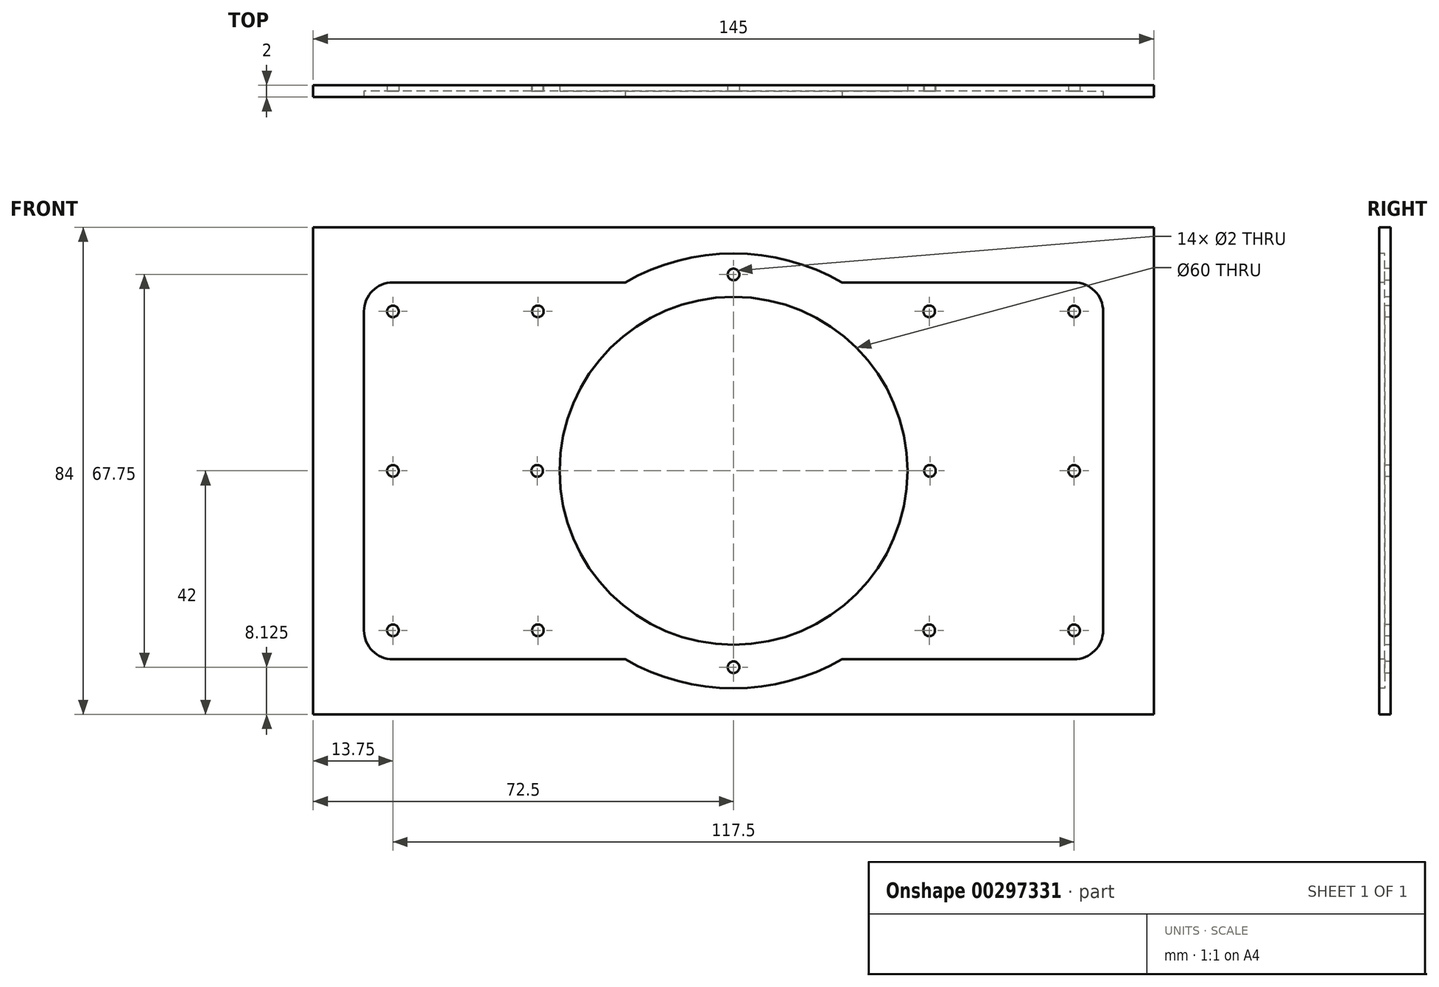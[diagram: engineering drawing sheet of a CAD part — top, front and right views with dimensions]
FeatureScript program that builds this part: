
annotation { "Feature Type Name" : "Feature", "Feature Type Description" : "" }
export const myFeature = defineFeature(function(context is Context, id is Id, definition is map)
    precondition{}
    {
        {
            var Q0;
            Q0=qCreatedBy(makeId("Front.planeOp"),FACE);
            var sketch = newSketch(context, id + "F0", { "sketchPlane" : qUnion([Q0])});
            skLineSegment(sketch, "E0.bottom", {"start": v(72.5, 42) * mm, "end": v(-72.5, 42) * mm});
            skLineSegment(sketch, "E0.top", {"start": v(72.5, -42) * mm, "end": v(-72.5, -42) * mm});
            skLineSegment(sketch, "E0.left", {"start": v(72.5, 42) * mm, "end": v(72.5, -42) * mm});
            skLineSegment(sketch, "E0.right", {"start": v(-72.5, 42) * mm, "end": v(-72.5, -42) * mm});
            skPoint(sketch, "E0.middle", {"position": v(0, 0) * mm});
            skSolve(sketch);
        }
        {
            var Q0;
            Q0 = qSketchRegion(id + "F0", true);
            extrude(context, id + "F1", {"entities" : qUnion([Q0]), "depth" : 2 * mm});
        }
        {
            var Q0;
            Q0=makeQuery(id+"F1.opExtrude","CAP_FACE",FACE,{"disambiguationData":[OSD([sQuery(id+"F0.wireOp",EDGE,"E0.bottom"),sQuery(id+"F0.wireOp",EDGE,"E0.top"),sQuery(id+"F0.wireOp",EDGE,"E0.left"),sQuery(id+"F0.wireOp",EDGE,"E0.right")])],"isStart":false});
            var sketch = newSketch(context, id + "F2", { "sketchPlane" : qUnion([Q0])});
            skCircle(sketch, "E1", {"center": v(0, 0) * mm, "radius": 37.5 * mm});
            skLineSegment(sketch, "E2.bottom", {"start": v(63.75, 32.5) * mm, "end": v(-63.75, 32.5) * mm});
            skLineSegment(sketch, "E2.top", {"start": v(63.75, -32.5) * mm, "end": v(-63.75, -32.5) * mm});
            skLineSegment(sketch, "E2.left", {"start": v(63.75, 32.5) * mm, "end": v(63.75, -32.5) * mm});
            skLineSegment(sketch, "E2.right", {"start": v(-63.75, 32.5) * mm, "end": v(-63.75, -32.5) * mm});
            skSolve(sketch);
        }
        {
            var Q0;
            Q0 = qSketchRegion(id + "F2", true);
            extrude(context, id + "F3", {"entities" : qUnion([Q0]), "operationType" : NewBodyOperationType.REMOVE, "oppositeDirection" : true, "depth" : 1 * mm});
        }
        {
            var Q0;
            Q0=makeQuery(id+"F3.boolean.opBoolean","COPY",FACE,{"derivedFrom":makeQuery(id+"F3.opExtrude","CAP_FACE",FACE,{"disambiguationData":[OSD([sQuery(id+"F2.wireOp",EDGE,"E1"),sQuery(id+"F2.wireOp",EDGE,"E2.bottom"),sQuery(id+"F2.wireOp",EDGE,"E2.top"),sQuery(id+"F2.wireOp",EDGE,"E2.left"),sQuery(id+"F2.wireOp",EDGE,"E2.right")])],"isStart":false})});
            var sketch = newSketch(context, id + "F4", { "sketchPlane" : qUnion([Q0])});
            skCircle(sketch, "E3", {"center": v(0, 0) * mm, "radius": 30 * mm});
            skSolve(sketch);
        }
        {
            var Q0;
            Q0 = qSketchRegion(id + "F4", true);
            extrude(context, id + "F5", {"entities" : qUnion([Q0]), "operationType" : NewBodyOperationType.REMOVE, "oppositeDirection" : true, "depth" : 25 * mm});
        }
        {
            var Q0;
            Q0=makeQuery(id+"F3.boolean.opBoolean","COPY",FACE,{"derivedFrom":makeQuery(id+"F3.opExtrude","CAP_FACE",FACE,{"disambiguationData":[OSD([sQuery(id+"F2.wireOp",EDGE,"E1"),sQuery(id+"F2.wireOp",EDGE,"E2.bottom"),sQuery(id+"F2.wireOp",EDGE,"E2.top"),sQuery(id+"F2.wireOp",EDGE,"E2.left"),sQuery(id+"F2.wireOp",EDGE,"E2.right")])],"isStart":false})});
            var sketch = newSketch(context, id + "F6", { "sketchPlane" : qUnion([Q0])});
            skLineSegment(sketch, "E4.bottom", {"start": v(58.75, 27.5) * mm, "end": v(-58.75, 27.5) * mm, "construction": true});
            skLineSegment(sketch, "E4.top", {"start": v(58.75, -27.5) * mm, "end": v(-58.75, -27.5) * mm, "construction": true});
            skLineSegment(sketch, "E4.left", {"start": v(58.75, 27.5) * mm, "end": v(58.75, -27.5) * mm, "construction": true});
            skLineSegment(sketch, "E4.right", {"start": v(-58.75, 27.5) * mm, "end": v(-58.75, -27.5) * mm, "construction": true});
            skPoint(sketch, "E4.middle", {"position": v(0, 0) * mm});
            skCircle(sketch, "E5", {"center": v(-58.75, 27.5) * mm, "radius": 1 * mm});
            skCircle(sketch, "E6", {"center": v(-58.75, -27.5) * mm, "radius": 1 * mm});
            skCircle(sketch, "E7", {"center": v(58.75, -27.5) * mm, "radius": 1 * mm});
            skCircle(sketch, "E8", {"center": v(58.75, 27.5) * mm, "radius": 1 * mm});
            skCircle(sketch, "E9", {"center": v(-58.75, 0) * mm, "radius": 1 * mm});
            skCircle(sketch, "E10", {"center": v(58.75, 0) * mm, "radius": 1 * mm});
            skCircle(sketch, "E11", {"center": v(-33.75, 27.5) * mm, "radius": 1 * mm});
            skCircle(sketch, "E12", {"center": v(33.75, 27.5) * mm, "radius": 1 * mm});
            skCircle(sketch, "E13", {"center": v(33.75, -27.5) * mm, "radius": 1 * mm});
            skCircle(sketch, "E14", {"center": v(-33.75, -27.5) * mm, "radius": 1 * mm});
            skSolve(sketch);
        }
        {
            var Q0;
            Q0 = qSketchRegion(id + "F6", true);
            extrude(context, id + "F7", {"entities" : qUnion([Q0]), "operationType" : NewBodyOperationType.REMOVE, "oppositeDirection" : true, "depth" : 25 * mm});
        }
        {
            var Q0;
            Q0=makeQuery(id+"F3.boolean.opBoolean","COPY",FACE,{"derivedFrom":makeQuery(id+"F3.opExtrude","CAP_FACE",FACE,{"disambiguationData":[OSD([sQuery(id+"F2.wireOp",EDGE,"E1"),sQuery(id+"F2.wireOp",EDGE,"E2.bottom"),sQuery(id+"F2.wireOp",EDGE,"E2.top"),sQuery(id+"F2.wireOp",EDGE,"E2.left"),sQuery(id+"F2.wireOp",EDGE,"E2.right")])],"isStart":false})});
            var sketch = newSketch(context, id + "F8", { "sketchPlane" : qUnion([Q0])});
            skCircle(sketch, "E15", {"center": v(0, 0) * mm, "radius": 33.88 * mm, "construction": true});
            skCircle(sketch, "E16", {"center": v(0, 33.88) * mm, "radius": 1 * mm});
            skCircle(sketch, "E17", {"center": v(33.88, 0) * mm, "radius": 1 * mm});
            skCircle(sketch, "E18", {"center": v(-33.88, 0) * mm, "radius": 1 * mm});
            skCircle(sketch, "E19", {"center": v(0, -33.88) * mm, "radius": 1 * mm});
            skSolve(sketch);
        }
        {
            var Q0;
            Q0 = qSketchRegion(id + "F8", true);
            extrude(context, id + "F9", {"entities" : qUnion([Q0]), "operationType" : NewBodyOperationType.REMOVE, "oppositeDirection" : true, "depth" : 25 * mm});
        }
        {
            var Q0;
            Q0=makeQuery(id+"F3.boolean.opBoolean","COPY",EDGE,{"derivedFrom":makeQuery(id+"F3.opExtrude","SWEPT_EDGE",EDGE,{"disambiguationData":[OSD([sQuery(id+"F2.wireOp",EDGE,"E2.bottom"),sQuery(id+"F2.wireOp",EDGE,"E2.right")])]})});
            var Q1;
            Q1=makeQuery(id+"F3.boolean.opBoolean","COPY",EDGE,{"derivedFrom":makeQuery(id+"F3.opExtrude","SWEPT_EDGE",EDGE,{"disambiguationData":[OSD([sQuery(id+"F2.wireOp",EDGE,"E2.top"),sQuery(id+"F2.wireOp",EDGE,"E2.right")])]})});
            var Q2;
            Q2=makeQuery(id+"F3.boolean.opBoolean","COPY",EDGE,{"derivedFrom":makeQuery(id+"F3.opExtrude","SWEPT_EDGE",EDGE,{"disambiguationData":[OSD([sQuery(id+"F2.wireOp",EDGE,"E2.bottom"),sQuery(id+"F2.wireOp",EDGE,"E2.left")])]})});
            var Q3;
            Q3=makeQuery(id+"F3.boolean.opBoolean","COPY",EDGE,{"derivedFrom":makeQuery(id+"F3.opExtrude","SWEPT_EDGE",EDGE,{"disambiguationData":[OSD([sQuery(id+"F2.wireOp",EDGE,"E2.top"),sQuery(id+"F2.wireOp",EDGE,"E2.left")])]})});
            fillet(context, id + "F10", {"entities" : qUnion([Q0, Q1, Q2, Q3]), "radius" : 5 * mm, "tangentPropagation" : true, "allowEdgeOverflow" : false});
        }
    });
